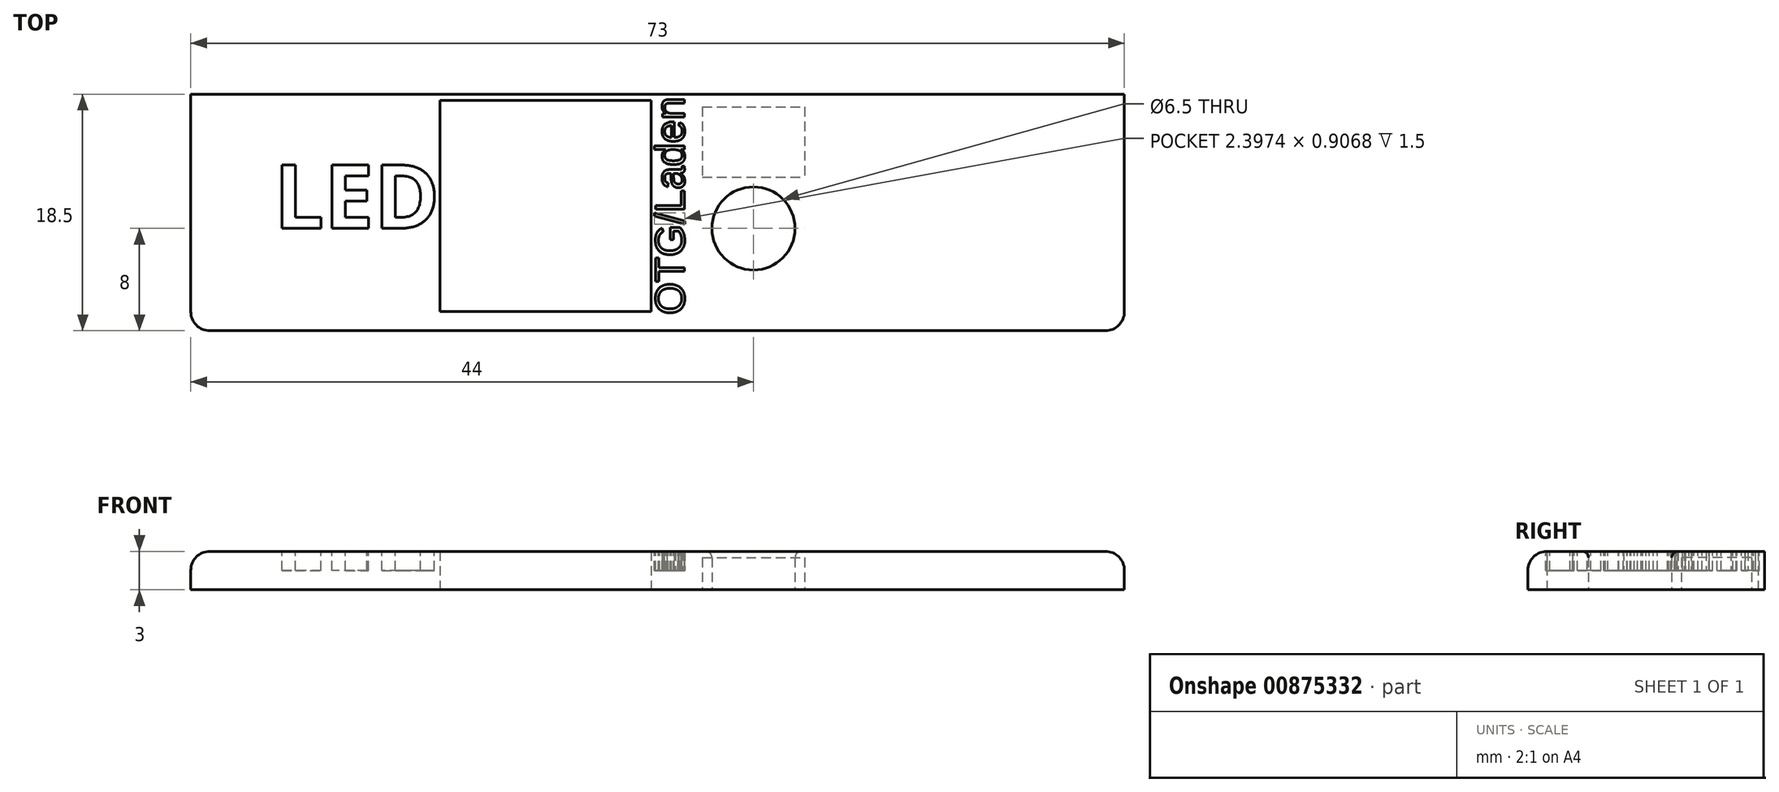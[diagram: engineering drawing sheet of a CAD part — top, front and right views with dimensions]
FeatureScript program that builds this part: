
annotation { "Feature Type Name" : "Feature", "Feature Type Description" : "" }
export const myFeature = defineFeature(function(context is Context, id is Id, definition is map)
    precondition{}
    {
        {
            var Q0;
            Q0=qCreatedBy(makeId("Top.planeOp"),FACE);
            var sketch = newSketch(context, id + "F0", { "sketchPlane" : qUnion([Q0])});
            skLineSegment(sketch, "E0.bottom", {"start": v(0, 0) * mm, "end": v(73, 0) * mm});
            skLineSegment(sketch, "E0.top", {"start": v(0, 23) * mm, "end": v(73, 23) * mm});
            skLineSegment(sketch, "E0.left", {"start": v(0, 0) * mm, "end": v(0, 23) * mm});
            skLineSegment(sketch, "E0.right", {"start": v(73, 0) * mm, "end": v(73, 23) * mm});
            skLineSegment(sketch, "E1.bottom", {"start": v(0, 23) * mm, "end": v(11.7, 23) * mm});
            skLineSegment(sketch, "E1.top", {"start": v(0, 18.5) * mm, "end": v(11.7, 18.5) * mm});
            skLineSegment(sketch, "E1.left", {"start": v(0, 23) * mm, "end": v(0, 18.5) * mm});
            skLineSegment(sketch, "E1.right", {"start": v(11.7, 23) * mm, "end": v(11.7, 18.5) * mm});
            skLineSegment(sketch, "E2.bottom", {"start": v(73, 23) * mm, "end": v(61.3, 23) * mm});
            skLineSegment(sketch, "E2.top", {"start": v(73, 18.5) * mm, "end": v(61.3, 18.5) * mm});
            skLineSegment(sketch, "E2.left", {"start": v(73, 23) * mm, "end": v(73, 18.5) * mm});
            skLineSegment(sketch, "E2.right", {"start": v(61.3, 23) * mm, "end": v(61.3, 18.5) * mm});
            skLineSegment(sketch, "E3.bottom", {"start": v(60.74, 23) * mm, "end": v(49.04, 23) * mm});
            skLineSegment(sketch, "E3.top", {"start": v(60.74, 18.5) * mm, "end": v(49.04, 18.5) * mm});
            skLineSegment(sketch, "E3.left", {"start": v(60.74, 23) * mm, "end": v(60.74, 18.5) * mm});
            skLineSegment(sketch, "E3.right", {"start": v(49.04, 23) * mm, "end": v(49.04, 18.5) * mm});
            skLineSegment(sketch, "E4.bottom", {"start": v(48.48, 23) * mm, "end": v(36.78, 23) * mm});
            skLineSegment(sketch, "E4.top", {"start": v(48.48, 18.5) * mm, "end": v(36.78, 18.5) * mm});
            skLineSegment(sketch, "E4.left", {"start": v(48.48, 23) * mm, "end": v(48.48, 18.5) * mm});
            skLineSegment(sketch, "E4.right", {"start": v(36.78, 23) * mm, "end": v(36.78, 18.5) * mm});
            skLineSegment(sketch, "E5.bottom", {"start": v(36.22, 23) * mm, "end": v(24.52, 23) * mm});
            skLineSegment(sketch, "E5.top", {"start": v(36.22, 18.5) * mm, "end": v(24.52, 18.5) * mm});
            skLineSegment(sketch, "E5.left", {"start": v(36.22, 23) * mm, "end": v(36.22, 18.5) * mm});
            skLineSegment(sketch, "E5.right", {"start": v(24.52, 23) * mm, "end": v(24.52, 18.5) * mm});
            skLineSegment(sketch, "E6.bottom", {"start": v(23.96, 23) * mm, "end": v(12.26, 23) * mm});
            skLineSegment(sketch, "E6.top", {"start": v(23.96, 18.5) * mm, "end": v(12.26, 18.5) * mm});
            skLineSegment(sketch, "E6.left", {"start": v(23.96, 23) * mm, "end": v(23.96, 18.5) * mm});
            skLineSegment(sketch, "E6.right", {"start": v(12.26, 23) * mm, "end": v(12.26, 18.5) * mm});
            skLineSegment(sketch, "E7", {"start": v(61.3, 18.5) * mm, "end": v(11.7, 18.5) * mm});
            skLineSegment(sketch, "E8.bottom", {"start": v(36, 1.5) * mm, "end": v(19.5, 1.5) * mm});
            skLineSegment(sketch, "E8.top", {"start": v(19.5, 18) * mm, "end": v(36, 18) * mm});
            skLineSegment(sketch, "E8.left", {"start": v(19.5, 1.5) * mm, "end": v(19.5, 18) * mm});
            skLineSegment(sketch, "E8.right", {"start": v(36, 1.5) * mm, "end": v(36, 18) * mm});
            skCircle(sketch, "E9", {"center": v(44, 8) * mm, "radius": 3.25 * mm});
            skLineSegment(sketch, "E10.bottom", {"start": v(40, 17.5) * mm, "end": v(48, 17.5) * mm});
            skLineSegment(sketch, "E10.top", {"start": v(40, 12) * mm, "end": v(48, 12) * mm});
            skLineSegment(sketch, "E10.left", {"start": v(40, 17.5) * mm, "end": v(40, 12) * mm});
            skLineSegment(sketch, "E10.right", {"start": v(48, 17.5) * mm, "end": v(48, 12) * mm});
            skSolve(sketch);
        }
        {
            var Q0;
            Q0=makeQuery(id+"F0.imprint","IMPRINT",FACE,{"disambiguationData":[TD([[makeQuery(id+"F0.imprint","IMPRINT",EDGE,{"derivedFrom":sQuery(id+"F0.wireOp",EDGE,"E0.bottom")}),1.0]])]});
            var Q1;
            Q1=makeQuery(id+"F0.imprint","IMPRINT",FACE,{"disambiguationData":[TD([[makeQuery(id+"F0.imprint","IMPRINT",EDGE,{"derivedFrom":sQuery(id+"F0.wireOp",EDGE,"E10.bottom")}),-1.0]])]});
            extrude(context, id + "F1", {"entities" : qUnion([Q0, Q1]), "depth" : 3 * mm, "offsetDistance" : 25 * mm});
        }
        {
            var Q0;
            Q0=makeQuery(id+"F0.imprint","IMPRINT",FACE,{"disambiguationData":[TD([[makeQuery(id+"F0.imprint","IMPRINT",EDGE,{"derivedFrom":sQuery(id+"F0.wireOp",EDGE,"E1.bottom")}),-1.0]])]});
            var Q1;
            Q1=makeQuery(id+"F0.imprint","IMPRINT",FACE,{"disambiguationData":[TD([[makeQuery(id+"F0.imprint","IMPRINT",EDGE,{"derivedFrom":sQuery(id+"F0.wireOp",EDGE,"E5.bottom")}),1.0]])]});
            var Q2;
            Q2=makeQuery(id+"F0.imprint","IMPRINT",FACE,{"disambiguationData":[TD([[makeQuery(id+"F0.imprint","IMPRINT",EDGE,{"derivedFrom":sQuery(id+"F0.wireOp",EDGE,"E3.bottom")}),1.0]])]});
            var Q3;
            {var subQ0=sQuery(id+"F0.wireOp",EDGE,"E2.right");Q3=makeQuery(id+"F0.imprint","IMPRINT",FACE,{"disambiguationData":[TD([[makeQuery(id+"F0.imprint","IMPRINT",EDGE,{"derivedFrom":subQ0}),-1.0]])]});}
            var Q4;
            {var subQ0=sQuery(id+"F0.wireOp",EDGE,"E3.right");Q4=makeQuery(id+"F0.imprint","IMPRINT",FACE,{"disambiguationData":[TD([[makeQuery(id+"F0.imprint","IMPRINT",EDGE,{"derivedFrom":subQ0}),-1.0]])]});}
            var Q5;
            {var subQ0=sQuery(id+"F0.wireOp",EDGE,"E4.right");Q5=makeQuery(id+"F0.imprint","IMPRINT",FACE,{"disambiguationData":[TD([[makeQuery(id+"F0.imprint","IMPRINT",EDGE,{"derivedFrom":subQ0}),-1.0]])]});}
            var Q6;
            {var subQ0=sQuery(id+"F0.wireOp",EDGE,"E5.right");Q6=makeQuery(id+"F0.imprint","IMPRINT",FACE,{"disambiguationData":[TD([[makeQuery(id+"F0.imprint","IMPRINT",EDGE,{"derivedFrom":subQ0}),-1.0]])]});}
            extrude(context, id + "F2", {"entities" : qUnion([Q0, Q1, Q2, Q3, Q4, Q5, Q6]), "operationType" : NewBodyOperationType.ADD, "depth" : 3 * mm, "offsetDistance" : 25 * mm});
        }
        {
            var Q0;
            Q0=makeQuery(id+"F2.opExtrude","SWEPT_FACE",FACE,{"disambiguationData":[OSD([sQuery(id+"F0.wireOp",EDGE,"E2.right")])]});
            var sketch = newSketch(context, id + "F3", { "sketchPlane" : qUnion([Q0])});
            skCircle(sketch, "E11", {"center": v(20.5, 1.1) * mm, "radius": 1.3 * mm});
            skLineSegment(sketch, "E12", {"start": v(19.2, 1.1) * mm, "end": v(19.2, 0) * mm});
            skLineSegment(sketch, "E13", {"start": v(21.8, 1.1) * mm, "end": v(21.8, 0) * mm});
            skSolve(sketch);
        }
        {
            var Q0;
            Q0=makeQuery(id+"F3.imprint","IMPRINT",FACE,{"disambiguationData":[TD([[makeQuery(id+"F3.imprint","IMPRINT",EDGE,{"derivedFrom":sQuery(id+"F3.wireOp",EDGE,"E11")}),1.0]])]});
            var Q1;
            {var subQ0=sQuery(id+"F3.wireOp",EDGE,"E12");Q1=makeQuery(id+"F3.imprint","IMPRINT",FACE,{"disambiguationData":[TD([[makeQuery(id+"F3.imprint","IMPRINT",EDGE,{"derivedFrom":subQ0}),1.0]])]});}
            var Q2;
            {var subQ0=sQuery(id+"F3.wireOp",EDGE,"E13");Q2=makeQuery(id+"F3.imprint","IMPRINT",FACE,{"disambiguationData":[TD([[makeQuery(id+"F3.imprint","IMPRINT",EDGE,{"derivedFrom":subQ0}),-1.0]])]});}
            extrude(context, id + "F4", {"entities" : qUnion([Q0, Q1, Q2]), "operationType" : NewBodyOperationType.REMOVE, "oppositeDirection" : true, "depth" : 62 * mm, "offsetDistance" : 25 * mm});
        }
        {
            var Q0;
            {var subQ0=sQuery(id+"F0.wireOp",EDGE,"E5.right");Q0=makeQuery(id+"F0.imprint","IMPRINT",FACE,{"disambiguationData":[TD([[makeQuery(id+"F0.imprint","IMPRINT",EDGE,{"derivedFrom":subQ0}),-1.0]])]});}
            var Q1;
            {var subQ0=sQuery(id+"F0.wireOp",EDGE,"E4.right");Q1=makeQuery(id+"F0.imprint","IMPRINT",FACE,{"disambiguationData":[TD([[makeQuery(id+"F0.imprint","IMPRINT",EDGE,{"derivedFrom":subQ0}),-1.0]])]});}
            var Q2;
            {var subQ0=sQuery(id+"F0.wireOp",EDGE,"E3.right");Q2=makeQuery(id+"F0.imprint","IMPRINT",FACE,{"disambiguationData":[TD([[makeQuery(id+"F0.imprint","IMPRINT",EDGE,{"derivedFrom":subQ0}),-1.0]])]});}
            var Q3;
            {var subQ0=sQuery(id+"F0.wireOp",EDGE,"E2.right");Q3=makeQuery(id+"F0.imprint","IMPRINT",FACE,{"disambiguationData":[TD([[makeQuery(id+"F0.imprint","IMPRINT",EDGE,{"derivedFrom":subQ0}),-1.0]])]});}
            var Q4;
            {var subQ0=sQuery(id+"F0.wireOp",EDGE,"E1.right");Q4=makeQuery(id+"F0.imprint","IMPRINT",FACE,{"disambiguationData":[TD([[makeQuery(id+"F0.imprint","IMPRINT",EDGE,{"derivedFrom":subQ0}),1.0]])]});}
            extrude(context, id + "F5", {"entities" : qUnion([Q0, Q1, Q2, Q3, Q4]), "operationType" : NewBodyOperationType.REMOVE, "depth" : 3 * mm, "offsetDistance" : 25 * mm});
        }
        {
            var Q0;
            Q0=makeQuery(id+"F2.opExtrude","CAP_EDGE",EDGE,{"disambiguationData":[OSD([sQuery(id+"F0.wireOp",EDGE,"E0.top"),sQuery(id+"F0.wireOp",EDGE,"E3.bottom")])],"isStart":false});
            var Q1;
            Q1=makeQuery(id+"F2.opExtrude","CAP_EDGE",EDGE,{"disambiguationData":[OSD([sQuery(id+"F0.wireOp",EDGE,"E0.top"),sQuery(id+"F0.wireOp",EDGE,"E5.bottom")])],"isStart":false});
            var Q2;
            Q2=makeQuery(id+"F2.opExtrude","CAP_EDGE",EDGE,{"disambiguationData":[OSD([sQuery(id+"F0.wireOp",EDGE,"E1.bottom")])],"isStart":false});
            var Q3;
            Q3=makeQuery(id+"F2.boolean.opBoolean","MERGE",EDGE,{"derivedFrom":[makeQuery(id+"F1.opExtrude","CAP_EDGE",EDGE,{"disambiguationData":[OSD([sQuery(id+"F0.wireOp",EDGE,"E0.left")])],"isStart":false}),makeQuery(id+"F2.opExtrude","CAP_EDGE",EDGE,{"disambiguationData":[OSD([sQuery(id+"F0.wireOp",EDGE,"E1.left")])],"isStart":false})]});
            var Q4;
            Q4=makeQuery(id+"F1.opExtrude","SWEPT_EDGE",EDGE,{"disambiguationData":[OSD([sQuery(id+"F0.wireOp",EDGE,"E0.bottom"),sQuery(id+"F0.wireOp",EDGE,"E0.left")])]});
            var Q5;
            Q5=makeQuery(id+"F1.opExtrude","CAP_EDGE",EDGE,{"disambiguationData":[OSD([sQuery(id+"F0.wireOp",EDGE,"E0.bottom")])],"isStart":false});
            var Q6;
            Q6=makeQuery(id+"F1.opExtrude","CAP_EDGE",EDGE,{"disambiguationData":[OSD([sQuery(id+"F0.wireOp",EDGE,"E0.right")])],"isStart":false});
            var Q7;
            Q7=makeQuery(id+"F1.opExtrude","SWEPT_EDGE",EDGE,{"disambiguationData":[OSD([sQuery(id+"F0.wireOp",EDGE,"E0.bottom"),sQuery(id+"F0.wireOp",EDGE,"E0.right")])]});
            fillet(context, id + "F6", {"entities" : qUnion([Q0, Q1, Q2, Q3, Q4, Q5, Q6, Q7]), "radius" : 1.5 * mm, "tangentPropagation" : true, "allowEdgeOverflow" : false});
        }
        {
            var Q0;
            {var subQ0=sQuery(id+"F0.wireOp",EDGE,"E7");var subQ3=sQuery(id+"F0.wireOp",EDGE,"E2.top");var subQ4=sQuery(id+"F0.wireOp",EDGE,"E1.top");var subQ5=sQuery(id+"F0.wireOp",EDGE,"E1.right");Q0=makeQuery(id+"F5.boolean.opBoolean","MERGE",EDGE,{"derivedFrom":[makeQuery(id+"F2.boolean.opBoolean","SPLIT",EDGE,{"disambiguationData":[TD([makeQuery(id+"F2.opExtrude","SWEPT_FACE",FACE,{"disambiguationData":[OSD([subQ5])]})])],"derivedFrom":makeQuery(id+"F1.opExtrude","CAP_EDGE",EDGE,{"disambiguationData":[OSD([subQ4,subQ3,subQ0])],"isStart":false})})],"fromTools":[makeQuery(id+"F5.opExtrude","CAP_EDGE",EDGE,{"disambiguationData":[OSD([subQ0]),TDD([makeQuery(id+"F0.imprint","IMPRINT",EDGE,{"disambiguationData":[TD([[makeQuery(id+"F0.imprint","INTERSECT",VERTEX,{"derivedFrom":[sQuery(id+"F0.wireOp",EDGE,"E5.right"),subQ0]}),-1.0]])],"derivedFrom":subQ0})])],"isStart":false})]});}
            var Q1;
            {var subQ0=sQuery(id+"F0.wireOp",EDGE,"E7");var subQ1=sQuery(id+"F0.wireOp",EDGE,"E4.right");var subQ2=sQuery(id+"F0.wireOp",EDGE,"E4.left");var subQ4=sQuery(id+"F0.wireOp",EDGE,"E2.top");var subQ5=sQuery(id+"F0.wireOp",EDGE,"E1.top");Q1=makeQuery(id+"F5.boolean.opBoolean","MERGE",EDGE,{"derivedFrom":[makeQuery(id+"F2.boolean.opBoolean","SPLIT",EDGE,{"disambiguationData":[TD([makeQuery(id+"F2.opExtrude","SWEPT_FACE",FACE,{"disambiguationData":[OSD([subQ2])]})])],"derivedFrom":makeQuery(id+"F1.opExtrude","CAP_EDGE",EDGE,{"disambiguationData":[OSD([subQ5,subQ4,subQ0])],"isStart":false})})],"fromTools":[makeQuery(id+"F5.opExtrude","CAP_EDGE",EDGE,{"disambiguationData":[OSD([subQ0]),TDD([makeQuery(id+"F0.imprint","IMPRINT",EDGE,{"disambiguationData":[TD([[makeQuery(id+"F0.imprint","INTERSECT",VERTEX,{"derivedFrom":[sQuery(id+"F0.wireOp",EDGE,"E3.right"),subQ0]}),-1.0]])],"derivedFrom":subQ0})])],"isStart":false}),makeQuery(id+"F5.opExtrude","CAP_EDGE",EDGE,{"disambiguationData":[OSD([subQ0]),TDD([makeQuery(id+"F0.imprint","IMPRINT",EDGE,{"disambiguationData":[TD([[makeQuery(id+"F0.imprint","INTERSECT",VERTEX,{"derivedFrom":[subQ1,subQ0]}),-1.0]])],"derivedFrom":subQ0})])],"isStart":false})]});}
            var Q2;
            {var subQ0=sQuery(id+"F0.wireOp",EDGE,"E7");var subQ2=sQuery(id+"F0.wireOp",EDGE,"E2.top");var subQ3=sQuery(id+"F0.wireOp",EDGE,"E1.top");var subQ5=sQuery(id+"F0.wireOp",EDGE,"E0.right");Q2=makeQuery(id+"F5.boolean.opBoolean","MERGE",EDGE,{"derivedFrom":[makeQuery(id+"F2.boolean.opBoolean","SPLIT",EDGE,{"disambiguationData":[TD([makeQuery(id+"F1.opExtrude","SWEPT_FACE",FACE,{"disambiguationData":[OSD([subQ5])]})])],"derivedFrom":makeQuery(id+"F1.opExtrude","CAP_EDGE",EDGE,{"disambiguationData":[OSD([subQ3,subQ2,subQ0])],"isStart":false})})],"fromTools":[makeQuery(id+"F5.opExtrude","CAP_EDGE",EDGE,{"disambiguationData":[OSD([subQ0]),TDD([makeQuery(id+"F0.imprint","IMPRINT",EDGE,{"disambiguationData":[TD([[makeQuery(id+"F0.imprint","INTERSECT",VERTEX,{"derivedFrom":[sQuery(id+"F0.wireOp",EDGE,"E3.left"),subQ0]}),1.0]])],"derivedFrom":subQ0})])],"isStart":false})]});}
            var Q3;
            Q3=makeQuery(id+"F5.boolean.opBoolean","COPY",EDGE,{"derivedFrom":makeQuery(id+"F5.opExtrude","CAP_EDGE",EDGE,{"disambiguationData":[OSD([sQuery(id+"F0.wireOp",EDGE,"E3.left")])],"isStart":false})});
            var Q4;
            Q4=makeQuery(id+"F5.boolean.opBoolean","COPY",EDGE,{"derivedFrom":makeQuery(id+"F5.opExtrude","CAP_EDGE",EDGE,{"disambiguationData":[OSD([sQuery(id+"F0.wireOp",EDGE,"E3.right")])],"isStart":false})});
            var Q5;
            Q5=makeQuery(id+"F5.boolean.opBoolean","COPY",EDGE,{"derivedFrom":makeQuery(id+"F5.opExtrude","CAP_EDGE",EDGE,{"disambiguationData":[OSD([sQuery(id+"F0.wireOp",EDGE,"E5.left")])],"isStart":false})});
            var Q6;
            Q6=makeQuery(id+"F5.boolean.opBoolean","COPY",EDGE,{"derivedFrom":makeQuery(id+"F5.opExtrude","CAP_EDGE",EDGE,{"disambiguationData":[OSD([sQuery(id+"F0.wireOp",EDGE,"E5.right")])],"isStart":false})});
            var Q7;
            Q7=makeQuery(id+"F2.opExtrude","CAP_EDGE",EDGE,{"disambiguationData":[OSD([sQuery(id+"F0.wireOp",EDGE,"E1.right")])],"isStart":false});
            var Q8;
            Q8=makeQuery(id+"F1.opExtrude","CAP_EDGE",EDGE,{"disambiguationData":[OSD([sQuery(id+"F0.wireOp",EDGE,"E9")])],"isStart":false});
            fillet(context, id + "F7", {"entities" : qUnion([Q0, Q1, Q2, Q3, Q4, Q5, Q6, Q7, Q8]), "radius" : 0.5 * mm, "tangentPropagation" : true, "allowEdgeOverflow" : false});
        }
        {
            var Q0;
            Q0=makeQuery(id+"F0.imprint","IMPRINT",FACE,{"disambiguationData":[TD([[makeQuery(id+"F0.imprint","IMPRINT",EDGE,{"derivedFrom":sQuery(id+"F0.wireOp",EDGE,"E10.bottom")}),-1.0]])]});
            extrude(context, id + "F8", {"entities" : qUnion([Q0]), "operationType" : NewBodyOperationType.REMOVE, "depth" : 2.5 * mm, "offsetDistance" : 25 * mm});
        }
        {
            var Q0;
            {var subQ0=sQuery(id+"F0.wireOp",EDGE,"E1.top");var subQ1=sQuery(id+"F0.wireOp",EDGE,"E7");var subQ2=sQuery(id+"F0.wireOp",EDGE,"E0.top");Q0=makeQuery(id+"F7.opFillet","SPLIT",FACE,{"disambiguationData":[OD(1.0)],"derivedFrom":makeQuery(id+"F2.boolean.opBoolean","MERGE",FACE,{"derivedFrom":[makeQuery(id+"F1.opExtrude","CAP_FACE",FACE,{"disambiguationData":[OSD([sQuery(id+"F0.wireOp",EDGE,"E0.bottom"),sQuery(id+"F0.wireOp",EDGE,"E0.left"),sQuery(id+"F0.wireOp",EDGE,"E0.right"),subQ0,sQuery(id+"F0.wireOp",EDGE,"E2.top"),subQ1,sQuery(id+"F0.wireOp",EDGE,"E8.bottom"),sQuery(id+"F0.wireOp",EDGE,"E8.top"),sQuery(id+"F0.wireOp",EDGE,"E8.left"),sQuery(id+"F0.wireOp",EDGE,"E8.right"),sQuery(id+"F0.wireOp",EDGE,"E9")])],"isStart":false}),makeQuery(id+"F2.opExtrude","CAP_FACE",FACE,{"disambiguationData":[OSD([subQ2,sQuery(id+"F0.wireOp",EDGE,"E4.right"),sQuery(id+"F0.wireOp",EDGE,"E5.bottom"),sQuery(id+"F0.wireOp",EDGE,"E6.left"),subQ1])],"isStart":false}),makeQuery(id+"F2.opExtrude","CAP_FACE",FACE,{"disambiguationData":[OSD([subQ2,sQuery(id+"F0.wireOp",EDGE,"E2.right"),sQuery(id+"F0.wireOp",EDGE,"E3.bottom"),sQuery(id+"F0.wireOp",EDGE,"E4.left"),subQ1])],"isStart":false}),makeQuery(id+"F2.opExtrude","CAP_FACE",FACE,{"disambiguationData":[OSD([sQuery(id+"F0.wireOp",EDGE,"E1.bottom"),subQ0,sQuery(id+"F0.wireOp",EDGE,"E1.left"),sQuery(id+"F0.wireOp",EDGE,"E1.right")])],"isStart":false})]})});}
            var sketch = newSketch(context, id + "F9", { "sketchPlane" : qUnion([Q0])});
            skText(sketch, "E14", { "text": "LED", "fontName": "OpenSans-Bold.ttf"});
            skText(sketch, "E15", { "text": "OTG/Laden\n", "fontName": "Arimo-Regular.ttf"});
            const initialGuessF9  = {"E14": [0.0065, 0.008, 1, 0, 0.005], "E15": [0.0386, 0.00125, 0, 1, 0.00235]};
            skSetInitialGuess(sketch, initialGuessF9);
            skSolve(sketch);
        }
        {
            var Q0;
            Q0=makeQuery(id+"F9.imprint","IMPRINT",FACE,{"disambiguationData":[TD([[makeQuery(id+"F9.imprint","IMPRINT",EDGE,{"derivedFrom":sQuery(id+"F9.wireOp",EDGE,"E14.sketch_text.stroke-0")}),-1.0]])]});
            var Q1;
            Q1=makeQuery(id+"F9.imprint","IMPRINT",FACE,{"disambiguationData":[TD([[makeQuery(id+"F9.imprint","IMPRINT",EDGE,{"derivedFrom":sQuery(id+"F9.wireOp",EDGE,"E14.sketch_text.stroke-6")}),-1.0]])]});
            var Q2;
            Q2=makeQuery(id+"F9.imprint","IMPRINT",FACE,{"disambiguationData":[TD([[makeQuery(id+"F9.imprint","IMPRINT",EDGE,{"derivedFrom":sQuery(id+"F9.wireOp",EDGE,"E14.sketch_text.stroke-18")}),-1.0]])]});
            extrude(context, id + "F10", {"entities" : qUnion([Q0, Q1, Q2]), "operationType" : NewBodyOperationType.REMOVE, "oppositeDirection" : true, "depth" : 1.5 * mm, "offsetDistance" : 25 * mm});
        }
        {
            var Q0;
            Q0 = qSketchRegion(id + "F9", true);
            extrude(context, id + "F11", {"entities" : qUnion([Q0]), "operationType" : NewBodyOperationType.REMOVE, "oppositeDirection" : true, "depth" : 1.5 * mm, "offsetDistance" : 25 * mm});
        }
    });
